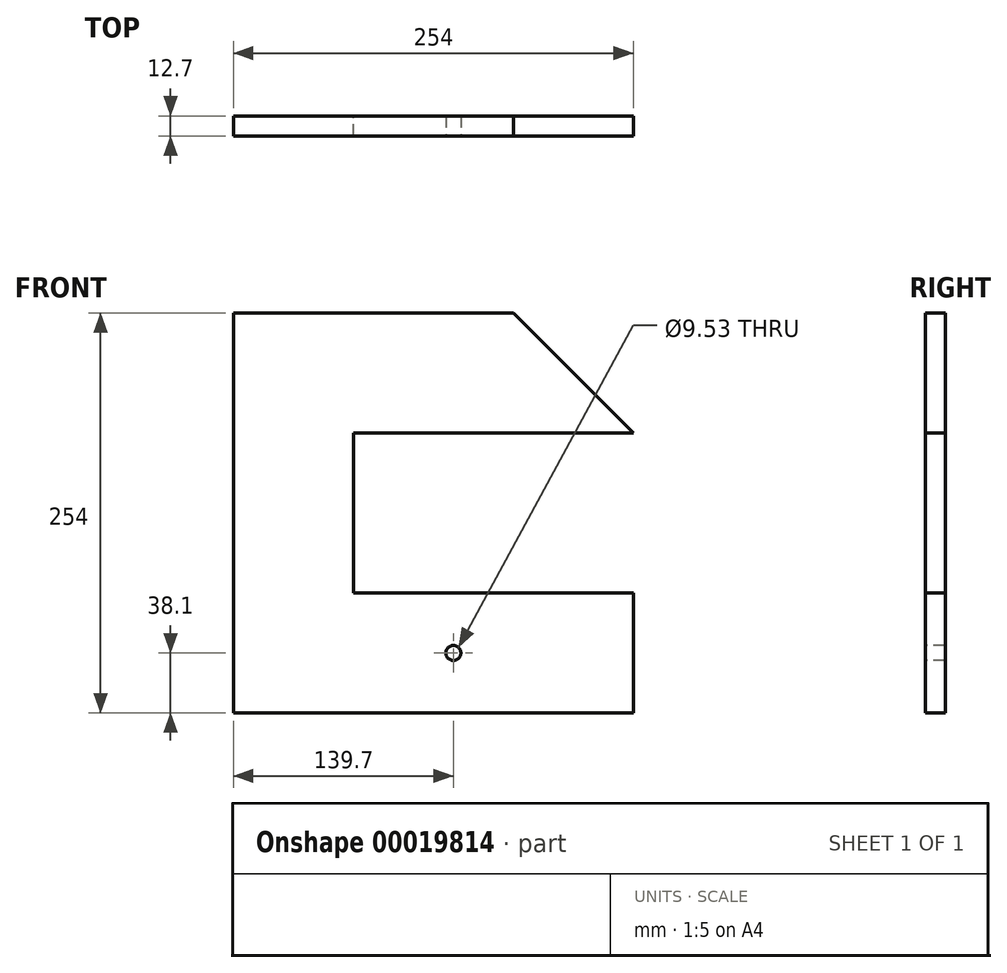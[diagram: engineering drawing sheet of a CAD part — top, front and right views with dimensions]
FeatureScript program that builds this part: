
annotation { "Feature Type Name" : "Feature", "Feature Type Description" : "" }
export const myFeature = defineFeature(function(context is Context, id is Id, definition is map)
    precondition{}
    {
        {
            var Q0;
            Q0=qCreatedBy(makeId("Front.planeOp"),FACE);
            var sketch = newSketch(context, id + "F0", { "sketchPlane" : qUnion([Q0])});
            skLineSegment(sketch, "E0", {"start": v(0, 254) * mm, "end": v(0, 0) * mm});
            skLineSegment(sketch, "E1", {"start": v(0, 0) * mm, "end": v(254, 0) * mm});
            skLineSegment(sketch, "E2", {"start": v(254, 0) * mm, "end": v(254, 76.2) * mm});
            skLineSegment(sketch, "E3", {"start": v(254, 76.2) * mm, "end": v(76.2, 76.2) * mm});
            skLineSegment(sketch, "E4", {"start": v(76.2, 76.2) * mm, "end": v(76.2, 177.8) * mm});
            skLineSegment(sketch, "E5", {"start": v(76.2, 177.8) * mm, "end": v(254, 177.8) * mm});
            skLineSegment(sketch, "E6", {"start": v(0, 254) * mm, "end": v(177.8, 254) * mm});
            skLineSegment(sketch, "E7", {"start": v(177.8, 254) * mm, "end": v(254, 177.8) * mm});
            skSolve(sketch);
        }
        {
            var Q0;
            Q0=qSketchRegion(id+"F0",true);
            extrude(context, id + "F1", {"entities" : qUnion([Q0]), "depth" : 12.7 * mm});
        }
        {
            var Q0;
            Q0=makeQuery(id+"F1.opExtrude","CAP_FACE",FACE,{"disambiguationData":[OSD([sQuery(id+"F0.wireOp",EDGE,"E0"),sQuery(id+"F0.wireOp",EDGE,"E1"),sQuery(id+"F0.wireOp",EDGE,"E2"),sQuery(id+"F0.wireOp",EDGE,"E3"),sQuery(id+"F0.wireOp",EDGE,"E4"),sQuery(id+"F0.wireOp",EDGE,"E5"),sQuery(id+"F0.wireOp",EDGE,"E6"),sQuery(id+"F0.wireOp",EDGE,"E7")])],"isStart":false});
            var sketch = newSketch(context, id + "F2", { "sketchPlane" : qUnion([Q0])});
            skPoint(sketch, "E8", {"position": v(139.7, 38.1) * mm});
            skSolve(sketch);
        }
        {
            var Q0;
            Q0=sQuery(id+"F2.wireOp",VERTEX,"E8");
            var Q1;
            Q1=makeQuery(id+"F1.opExtrude","SWEPT_BODY",BODY,{"disambiguationData":[OSD([sQuery(id+"F0.wireOp",EDGE,"E0"),sQuery(id+"F0.wireOp",EDGE,"E1"),sQuery(id+"F0.wireOp",EDGE,"E2"),sQuery(id+"F0.wireOp",EDGE,"E3"),sQuery(id+"F0.wireOp",EDGE,"E4"),sQuery(id+"F0.wireOp",EDGE,"E5"),sQuery(id+"F0.wireOp",EDGE,"E6"),sQuery(id+"F0.wireOp",EDGE,"E7")])]});
            hole(context, id + "F3", {"style" : HoleStyle.SIMPLE, "holeDiameter" : 9.52 * mm, "endStyle" : HoleEndStyle.THROUGH, "locations" : qUnion([Q0]), "scope" : qUnion([Q1])});
        }
    });
